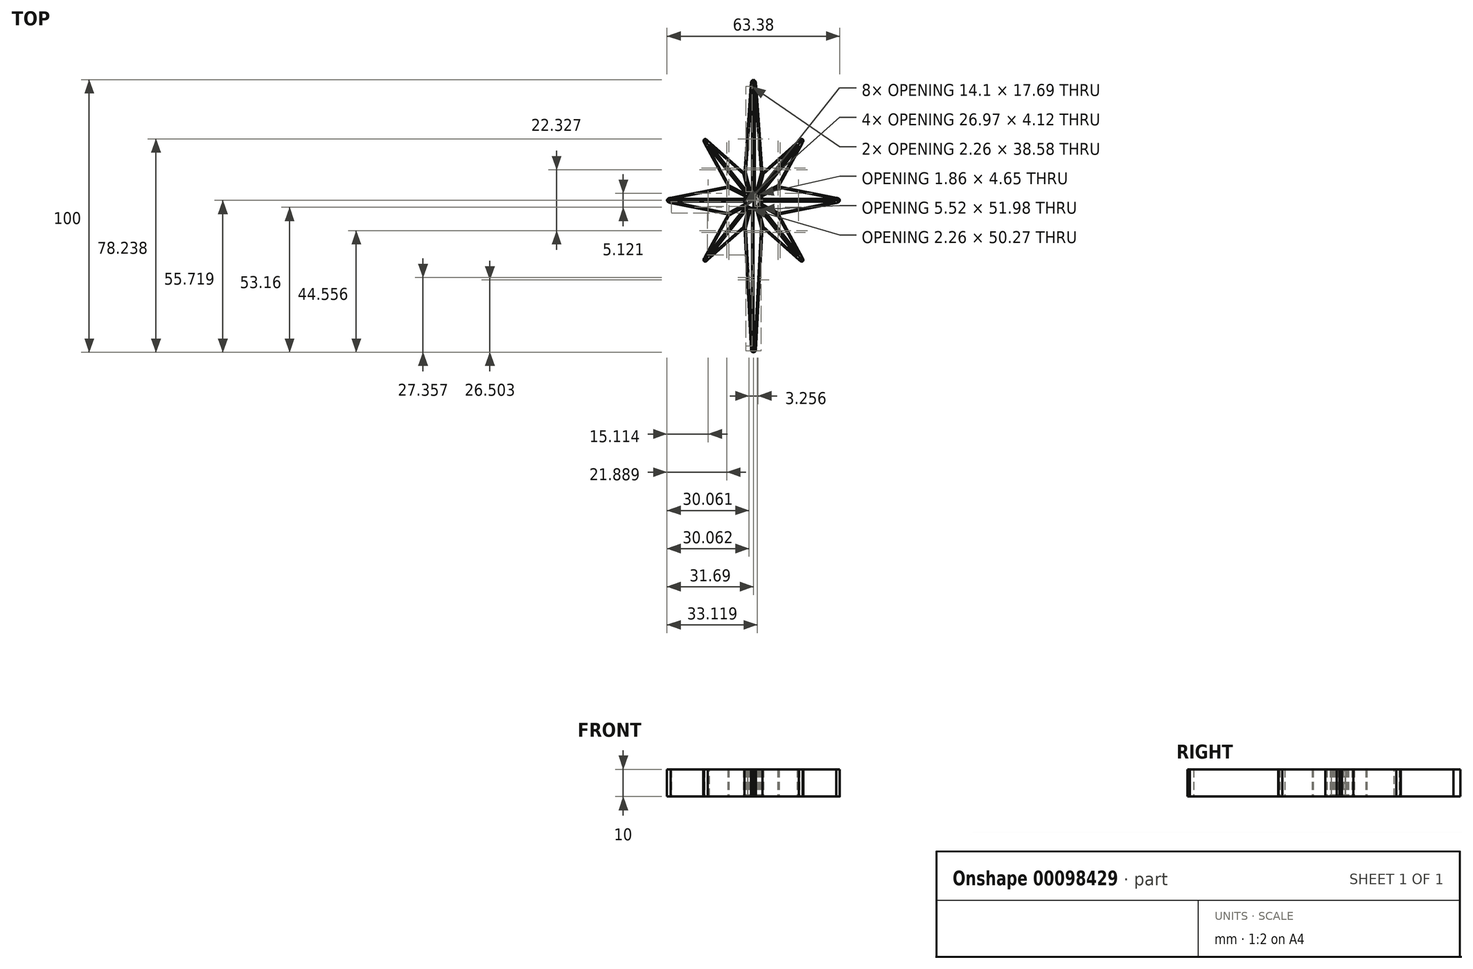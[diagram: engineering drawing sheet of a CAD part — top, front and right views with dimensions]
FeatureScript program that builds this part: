
annotation { "Feature Type Name" : "Feature", "Feature Type Description" : "" }
export const myFeature = defineFeature(function(context is Context, id is Id, definition is map)
    precondition{}
    {
        {
            var Q0;
            Q0=qCreatedBy(makeId("Top.planeOp"),FACE);
            var sketch = newSketch(context, id + "F0", { "sketchPlane" : qUnion([Q0])});
            skFitSpline(sketch, "E0", {"points": [v(0, 44.28) * mm, v(0.72, 43.7) * mm, v(1, 41.85) * mm], "startDerivative": vector(2.03, -1.03) * mm, "endDerivative": vector(0.73, -6.27) * mm});
            skLineSegment(sketch, "E1", {"start": v(1, 41.85) * mm, "end": v(3.26, 9.97) * mm});
            skLineSegment(sketch, "E2", {"start": v(3.26, 9.97) * mm, "end": v(1.35, 2.55) * mm});
            skLineSegment(sketch, "E3", {"start": v(0, -55.72) * mm, "end": v(0, 44.28) * mm});
            skFitSpline(sketch, "E4", {"points": [v(1.35, 2.55) * mm, v(0.8, 2.76) * mm, v(0, 2.88) * mm], "startDerivative": vector(-0.62, 0.31) * mm, "endDerivative": vector(-1.58, 0.08) * mm});
            skCircle(sketch, "E5", {"center": v(0, 0) * mm, "radius": 2.88 * mm});
            skFitSpline(sketch, "E6.MirrorCS", {"points": [v(0, 44.28) * mm, v(-0.72, 43.7) * mm, v(-1, 41.85) * mm], "startDerivative": vector(-2.03, -1.03) * mm, "endDerivative": vector(-0.73, -6.27) * mm});
            skLineSegment(sketch, "E7.MirrorCS", {"start": v(-1, 41.85) * mm, "end": v(-3.26, 9.97) * mm});
            skLineSegment(sketch, "E8.MirrorCS", {"start": v(-3.26, 9.97) * mm, "end": v(-1.35, 2.55) * mm});
            skLineSegment(sketch, "E9", {"start": v(-1.95, 2.12) * mm, "end": v(-18.09, 22.36) * mm});
            skFitSpline(sketch, "E10", {"points": [v(-18.09, 22.36) * mm, v(-17.59, 22.5) * mm, v(-16.7, 21.85) * mm], "startDerivative": vector(1.18, 0.65) * mm, "endDerivative": vector(1.58, -1.52) * mm});
            skLineSegment(sketch, "E11", {"start": v(-16.7, 21.85) * mm, "end": v(-3.26, 9.97) * mm});
            skFitSpline(sketch, "E12.MirrorCS", {"points": [v(-18.09, 22.36) * mm, v(-18.34, 21.9) * mm, v(-17.9, 20.9) * mm], "startDerivative": vector(-0.9, -1) * mm, "endDerivative": vector(1.14, -1.88) * mm});
            skLineSegment(sketch, "E13.MirrorCS", {"start": v(-17.9, 20.9) * mm, "end": v(-9.31, 5.15) * mm});
            skLineSegment(sketch, "E14.MirrorCS", {"start": v(-9.31, 5.15) * mm, "end": v(-2.4, 1.58) * mm});
            skPoint(sketch, "E15.orphan", {"position": v(-2.5, 1.63) * mm});
            skFitSpline(sketch, "E16", {"points": [v(-2.4, 1.58) * mm, v(-2.2, 1.85) * mm, v(-1.95, 2.12) * mm], "startDerivative": vector(0.4, 0.57) * mm, "endDerivative": vector(0.52, 0.51) * mm});
            skLineSegment(sketch, "E17.MirrorCS", {"start": v(16.7, 21.85) * mm, "end": v(3.26, 9.97) * mm});
            skFitSpline(sketch, "E18.MirrorCS", {"points": [v(18.09, 22.36) * mm, v(17.59, 22.5) * mm, v(16.7, 21.85) * mm], "startDerivative": vector(-1.18, 0.65) * mm, "endDerivative": vector(-1.58, -1.52) * mm});
            skFitSpline(sketch, "E19.MirrorCS", {"points": [v(18.09, 22.36) * mm, v(18.34, 21.9) * mm, v(17.9, 20.9) * mm], "startDerivative": vector(0.9, -1) * mm, "endDerivative": vector(-1.14, -1.88) * mm});
            skLineSegment(sketch, "E20.MirrorCS", {"start": v(17.9, 20.9) * mm, "end": v(9.31, 5.15) * mm});
            skLineSegment(sketch, "E21.MirrorCS", {"start": v(1.95, 2.12) * mm, "end": v(18.09, 22.36) * mm});
            skLineSegment(sketch, "E22.MirrorCS", {"start": v(9.31, 5.15) * mm, "end": v(2.4, 1.58) * mm});
            skLineSegment(sketch, "E23.MirrorCS", {"start": v(-9.31, -5.15) * mm, "end": v(-2.4, -1.58) * mm});
            skLineSegment(sketch, "E24.MirrorCS", {"start": v(-1.95, -2.12) * mm, "end": v(-18.09, -22.36) * mm});
            skLineSegment(sketch, "E25.MirrorCS", {"start": v(-17.9, -20.9) * mm, "end": v(-9.31, -5.15) * mm});
            skLineSegment(sketch, "E26.MirrorCS", {"start": v(-16.7, -21.85) * mm, "end": v(-3.26, -9.97) * mm});
            skLineSegment(sketch, "E27.MirrorCS", {"start": v(-3.26, -9.97) * mm, "end": v(-1.35, -2.55) * mm});
            skFitSpline(sketch, "E28.MirrorCS", {"points": [v(-18.09, -22.36) * mm, v(-18.34, -21.9) * mm, v(-17.9, -20.9) * mm], "startDerivative": vector(-0.9, 1) * mm, "endDerivative": vector(1.14, 1.88) * mm});
            skLineSegment(sketch, "E29.MirrorCS", {"start": v(16.7, -21.85) * mm, "end": v(3.26, -9.97) * mm});
            skLineSegment(sketch, "E30.MirrorCS", {"start": v(3.26, -9.97) * mm, "end": v(1.35, -2.55) * mm});
            skLineSegment(sketch, "E31.MirrorCS", {"start": v(1.95, -2.12) * mm, "end": v(18.09, -22.36) * mm});
            skLineSegment(sketch, "E32.MirrorCS", {"start": v(9.31, -5.15) * mm, "end": v(2.4, -1.58) * mm});
            skLineSegment(sketch, "E33.MirrorCS", {"start": v(17.9, -20.9) * mm, "end": v(9.31, -5.15) * mm});
            skFitSpline(sketch, "E34.MirrorCS", {"points": [v(18.09, -22.36) * mm, v(17.59, -22.5) * mm, v(16.7, -21.85) * mm], "startDerivative": vector(-1.18, -0.65) * mm, "endDerivative": vector(-1.58, 1.52) * mm});
            skFitSpline(sketch, "E35.MirrorCS", {"points": [v(18.09, -22.36) * mm, v(18.34, -21.9) * mm, v(17.9, -20.9) * mm], "startDerivative": vector(0.9, 1) * mm, "endDerivative": vector(-1.14, 1.88) * mm});
            skPoint(sketch, "E36.orphan", {"position": v(3.26, -9.97) * mm});
            skFitSpline(sketch, "E37.MirrorCS", {"points": [v(-18.09, -22.36) * mm, v(-17.59, -22.5) * mm, v(-16.7, -21.85) * mm], "startDerivative": vector(1.18, -0.65) * mm, "endDerivative": vector(1.58, 1.52) * mm});
            skLineSegment(sketch, "E38", {"start": v(-9.31, 5.15) * mm, "end": v(-30.36, 0.95) * mm});
            skFitSpline(sketch, "E39", {"points": [v(-30.36, 0.95) * mm, v(-31.49, 0.49) * mm, v(-31.69, 0) * mm, v(-31.67, 0) * mm], "startDerivative": vector(-2.54, -0.48) * mm, "endDerivative": vector(0.26, 0.12) * mm});
            skLineSegment(sketch, "E40", {"start": v(-31.67, 0) * mm, "end": v(-2.88, 0) * mm});
            skLineSegment(sketch, "E41.MirrorCS", {"start": v(-9.31, -5.15) * mm, "end": v(-30.36, -0.95) * mm});
            skFitSpline(sketch, "E42.MirrorCS", {"points": [v(-30.36, -0.95) * mm, v(-31.49, -0.49) * mm, v(-31.69, 0) * mm, v(-31.67, 0) * mm], "startDerivative": vector(-2.54, 0.48) * mm, "endDerivative": vector(0.26, -0.12) * mm});
            skLineSegment(sketch, "E43.MirrorCS", {"start": v(9.31, 5.15) * mm, "end": v(30.36, 0.95) * mm});
            skLineSegment(sketch, "E44.MirrorCS", {"start": v(9.31, -5.15) * mm, "end": v(30.36, -0.95) * mm});
            skFitSpline(sketch, "E45.MirrorCS", {"points": [v(30.36, -0.95) * mm, v(31.49, -0.49) * mm, v(31.69, 0) * mm, v(31.67, 0) * mm], "startDerivative": vector(2.54, 0.48) * mm, "endDerivative": vector(-0.26, -0.12) * mm});
            skFitSpline(sketch, "E46.MirrorCS", {"points": [v(30.36, 0.95) * mm, v(31.49, 0.49) * mm, v(31.69, 0) * mm, v(31.67, 0) * mm], "startDerivative": vector(2.54, -0.48) * mm, "endDerivative": vector(-0.26, 0.12) * mm});
            skLineSegment(sketch, "E47", {"start": v(31.69, 0) * mm, "end": v(2.88, 0) * mm});
            skLineSegment(sketch, "E48", {"start": v(-3.26, -9.97) * mm, "end": v(-0.93, -54.83) * mm});
            skFitSpline(sketch, "E49", {"points": [v(-0.93, -54.83) * mm, v(-0.72, -55.44) * mm, v(0, -55.72) * mm], "startDerivative": vector(0.23, -1.45) * mm, "endDerivative": vector(1.62, -0.34) * mm});
            skFitSpline(sketch, "E50.MirrorCS", {"points": [v(0.93, -54.83) * mm, v(0.72, -55.44) * mm, v(0, -55.72) * mm], "startDerivative": vector(-0.23, -1.45) * mm, "endDerivative": vector(-1.62, -0.34) * mm});
            skLineSegment(sketch, "E51.MirrorCS", {"start": v(3.26, -9.97) * mm, "end": v(0.93, -54.83) * mm});
            skLineSegment(sketch, "E52", {"start": v(0, -2.88) * mm, "end": v(0, -55.72) * mm});
            skSolve(sketch);
        }
        {
            var Q0;
            {var subQ1=sQuery(id+"F0.wireOp",EDGE,"E3");Q0=makeQuery(id+"F0.imprint","IMPRINT",FACE,{"disambiguationData":[TD([[makeQuery(id+"F0.imprint","IMPRINT",EDGE,{"derivedFrom":subQ1}),1.0]])]});}
            var Q1;
            {var subQ1=sQuery(id+"F0.wireOp",EDGE,"E2");Q1=makeQuery(id+"F0.imprint","IMPRINT",FACE,{"disambiguationData":[TD([[makeQuery(id+"F0.imprint","IMPRINT",EDGE,{"derivedFrom":subQ1}),1.0]])]});}
            var Q2;
            {var subQ7=sQuery(id+"F0.wireOp",EDGE,"E22.MirrorCS");Q2=makeQuery(id+"F0.imprint","IMPRINT",FACE,{"disambiguationData":[TD([[makeQuery(id+"F0.imprint","IMPRINT",EDGE,{"derivedFrom":subQ7}),1.0]])]});}
            var Q3;
            {var subQ0=sQuery(id+"F0.wireOp",EDGE,"E30.MirrorCS");Q3=makeQuery(id+"F0.imprint","IMPRINT",FACE,{"disambiguationData":[TD([[makeQuery(id+"F0.imprint","IMPRINT",EDGE,{"derivedFrom":subQ0}),1.0]])]});}
            extrude(context, id + "F1", {"entities" : qUnion([Q0, Q1, Q2, Q3]), "depth" : 10 * mm});
        }
        {
            var Q0;
            {var subQ0=sQuery(id+"F0.wireOp",EDGE,"E16");var subQ1=sQuery(id+"F0.wireOp",EDGE,"E5");var subQ13=makeQuery(id+"F0.imprint","INTERSECT",VERTEX,{"disambiguationData":[OD(0.0)],"derivedFrom":[subQ1,subQ0]});Q0=makeQuery(id+"F0.imprint","IMPRINT",FACE,{"disambiguationData":[TD([[makeQuery(id+"F0.imprint","IMPRINT",EDGE,{"disambiguationData":[TD([[subQ13,-1.0]])],"derivedFrom":subQ1}),1.0]])]});}
            var Q1;
            {var subQ4=sQuery(id+"F0.wireOp",EDGE,"E4");Q1=makeQuery(id+"F0.imprint","IMPRINT",FACE,{"disambiguationData":[TD([[makeQuery(id+"F0.imprint","IMPRINT",EDGE,{"derivedFrom":subQ4}),1.0]])]});}
            extrude(context, id + "F2", {"entities" : qUnion([Q0, Q1]), "depth" : 10 * mm});
        }
        {
            var Q0;
            Q0=makeQuery(id+"F1.opExtrude","CAP_FACE",FACE,{"disambiguationData":[OSD([sQuery(id+"F0.wireOp",EDGE,"E3"),sQuery(id+"F0.wireOp",EDGE,"E5"),sQuery(id+"F0.wireOp",EDGE,"E6.MirrorCS"),sQuery(id+"F0.wireOp",EDGE,"E7.MirrorCS"),sQuery(id+"F0.wireOp",EDGE,"E8.MirrorCS")])],"isStart":false});
            var Q1;
            Q1=makeQuery(id+"F1.opExtrude","CAP_FACE",FACE,{"disambiguationData":[OSD([sQuery(id+"F0.wireOp",EDGE,"E3"),sQuery(id+"F0.wireOp",EDGE,"E5"),sQuery(id+"F0.wireOp",EDGE,"E6.MirrorCS"),sQuery(id+"F0.wireOp",EDGE,"E7.MirrorCS"),sQuery(id+"F0.wireOp",EDGE,"E8.MirrorCS")])],"isStart":true});
            shell(context, id + "F3", {"entities" : qUnion([Q0, Q1]), "thickness" : .5 * mm});
        }
        {
            var Q0;
            {var subQ1=sQuery(id+"F0.wireOp",EDGE,"E0");Q0=makeQuery(id+"F0.imprint","IMPRINT",FACE,{"disambiguationData":[TD([[makeQuery(id+"F0.imprint","IMPRINT",EDGE,{"derivedFrom":subQ1}),-1.0]])]});}
            extrude(context, id + "F4", {"entities" : qUnion([Q0]), "depth" : 10 * mm});
        }
        {
            var Q0;
            Q0=makeQuery(id+"F4.opExtrude","CAP_FACE",FACE,{"disambiguationData":[OSD([sQuery(id+"F0.wireOp",EDGE,"E0"),sQuery(id+"F0.wireOp",EDGE,"E1"),sQuery(id+"F0.wireOp",EDGE,"E2"),sQuery(id+"F0.wireOp",EDGE,"E3"),sQuery(id+"F0.wireOp",EDGE,"E5")])],"isStart":false});
            var Q1;
            Q1=makeQuery(id+"F4.opExtrude","CAP_FACE",FACE,{"disambiguationData":[OSD([sQuery(id+"F0.wireOp",EDGE,"E0"),sQuery(id+"F0.wireOp",EDGE,"E1"),sQuery(id+"F0.wireOp",EDGE,"E2"),sQuery(id+"F0.wireOp",EDGE,"E3"),sQuery(id+"F0.wireOp",EDGE,"E5")])],"isStart":true});
            shell(context, id + "F5", {"entities" : qUnion([Q0, Q1]), "thickness" : .5 * mm});
        }
        {
            var Q0;
            Q0=makeQuery(id+"F1.opExtrude","CAP_FACE",FACE,{"disambiguationData":[OSD([sQuery(id+"F0.wireOp",EDGE,"E2"),sQuery(id+"F0.wireOp",EDGE,"E5"),sQuery(id+"F0.wireOp",EDGE,"E17.MirrorCS"),sQuery(id+"F0.wireOp",EDGE,"E18.MirrorCS"),sQuery(id+"F0.wireOp",EDGE,"E21.MirrorCS")])],"isStart":false});
            var Q1;
            Q1=makeQuery(id+"F1.opExtrude","CAP_FACE",FACE,{"disambiguationData":[OSD([sQuery(id+"F0.wireOp",EDGE,"E2"),sQuery(id+"F0.wireOp",EDGE,"E5"),sQuery(id+"F0.wireOp",EDGE,"E17.MirrorCS"),sQuery(id+"F0.wireOp",EDGE,"E18.MirrorCS"),sQuery(id+"F0.wireOp",EDGE,"E21.MirrorCS")])],"isStart":true});
            shell(context, id + "F6", {"entities" : qUnion([Q0, Q1]), "thickness" : .5 * mm});
        }
        {
            var Q0;
            Q0=makeQuery(id+"F2.opExtrude","CAP_FACE",FACE,{"disambiguationData":[OSD([sQuery(id+"F0.wireOp",EDGE,"E4"),sQuery(id+"F0.wireOp",EDGE,"E5"),sQuery(id+"F0.wireOp",EDGE,"E16")])],"isStart":false});
            var Q1;
            Q1=makeQuery(id+"F2.opExtrude","CAP_FACE",FACE,{"disambiguationData":[OSD([sQuery(id+"F0.wireOp",EDGE,"E4"),sQuery(id+"F0.wireOp",EDGE,"E5"),sQuery(id+"F0.wireOp",EDGE,"E16")])],"isStart":true});
            shell(context, id + "F7", {"entities" : qUnion([Q0, Q1]), "thickness" : .5 * mm});
        }
        {
            var Q0;
            Q0=makeQuery(id+"F0.imprint","IMPRINT",FACE,{"disambiguationData":[TD([[makeQuery(id+"F0.imprint","IMPRINT",EDGE,{"derivedFrom":sQuery(id+"F0.wireOp",EDGE,"E19.MirrorCS")}),-1.0]])]});
            extrude(context, id + "F8", {"entities" : qUnion([Q0]), "depth" : 10 * mm});
        }
        {
            var Q0;
            Q0=makeQuery(id+"F1.opExtrude","CAP_FACE",FACE,{"disambiguationData":[OSD([sQuery(id+"F0.wireOp",EDGE,"E5"),sQuery(id+"F0.wireOp",EDGE,"E22.MirrorCS"),sQuery(id+"F0.wireOp",EDGE,"E43.MirrorCS"),sQuery(id+"F0.wireOp",EDGE,"E45.MirrorCS"),sQuery(id+"F0.wireOp",EDGE,"E46.MirrorCS"),sQuery(id+"F0.wireOp",EDGE,"E47")])],"isStart":false});
            var Q1;
            Q1=makeQuery(id+"F1.opExtrude","CAP_FACE",FACE,{"disambiguationData":[OSD([sQuery(id+"F0.wireOp",EDGE,"E5"),sQuery(id+"F0.wireOp",EDGE,"E22.MirrorCS"),sQuery(id+"F0.wireOp",EDGE,"E43.MirrorCS"),sQuery(id+"F0.wireOp",EDGE,"E45.MirrorCS"),sQuery(id+"F0.wireOp",EDGE,"E46.MirrorCS"),sQuery(id+"F0.wireOp",EDGE,"E47")])],"isStart":true});
            shell(context, id + "F9", {"entities" : qUnion([Q0, Q1]), "thickness" : .5 * mm});
        }
        {
            var Q0;
            Q0=makeQuery(id+"F8.opExtrude","CAP_FACE",FACE,{"disambiguationData":[OSD([sQuery(id+"F0.wireOp",EDGE,"E5"),sQuery(id+"F0.wireOp",EDGE,"E19.MirrorCS"),sQuery(id+"F0.wireOp",EDGE,"E20.MirrorCS"),sQuery(id+"F0.wireOp",EDGE,"E21.MirrorCS"),sQuery(id+"F0.wireOp",EDGE,"E22.MirrorCS")])],"isStart":false});
            var Q1;
            Q1=makeQuery(id+"F8.opExtrude","CAP_FACE",FACE,{"disambiguationData":[OSD([sQuery(id+"F0.wireOp",EDGE,"E5"),sQuery(id+"F0.wireOp",EDGE,"E19.MirrorCS"),sQuery(id+"F0.wireOp",EDGE,"E20.MirrorCS"),sQuery(id+"F0.wireOp",EDGE,"E21.MirrorCS"),sQuery(id+"F0.wireOp",EDGE,"E22.MirrorCS")])],"isStart":true});
            shell(context, id + "F10", {"entities" : qUnion([Q0, Q1]), "thickness" : .5 * mm});
        }
        {
            var Q0;
            {var subQ5=sQuery(id+"F0.wireOp",EDGE,"E32.MirrorCS");Q0=makeQuery(id+"F0.imprint","IMPRINT",FACE,{"disambiguationData":[TD([[makeQuery(id+"F0.imprint","IMPRINT",EDGE,{"derivedFrom":subQ5}),-1.0]])]});}
            extrude(context, id + "F11", {"entities" : qUnion([Q0]), "depth" : 10 * mm});
        }
        {
            var Q0;
            Q0=makeQuery(id+"F11.opExtrude","CAP_FACE",FACE,{"disambiguationData":[OSD([sQuery(id+"F0.wireOp",EDGE,"E5"),sQuery(id+"F0.wireOp",EDGE,"E32.MirrorCS"),sQuery(id+"F0.wireOp",EDGE,"E44.MirrorCS"),sQuery(id+"F0.wireOp",EDGE,"E45.MirrorCS"),sQuery(id+"F0.wireOp",EDGE,"E46.MirrorCS"),sQuery(id+"F0.wireOp",EDGE,"E47")])],"isStart":false});
            var Q1;
            Q1=makeQuery(id+"F11.opExtrude","CAP_FACE",FACE,{"disambiguationData":[OSD([sQuery(id+"F0.wireOp",EDGE,"E5"),sQuery(id+"F0.wireOp",EDGE,"E32.MirrorCS"),sQuery(id+"F0.wireOp",EDGE,"E44.MirrorCS"),sQuery(id+"F0.wireOp",EDGE,"E45.MirrorCS"),sQuery(id+"F0.wireOp",EDGE,"E46.MirrorCS"),sQuery(id+"F0.wireOp",EDGE,"E47")])],"isStart":true});
            shell(context, id + "F12", {"entities" : qUnion([Q0, Q1]), "thickness" : .5 * mm});
        }
        {
            var Q0;
            {var subQ1=sQuery(id+"F0.wireOp",EDGE,"E31.MirrorCS");Q0=makeQuery(id+"F0.imprint","IMPRINT",FACE,{"disambiguationData":[TD([[makeQuery(id+"F0.imprint","IMPRINT",EDGE,{"derivedFrom":subQ1}),1.0]])]});}
            extrude(context, id + "F13", {"entities" : qUnion([Q0]), "depth" : 10 * mm});
        }
        {
            var Q0;
            Q0=makeQuery(id+"F13.opExtrude","CAP_FACE",FACE,{"disambiguationData":[OSD([sQuery(id+"F0.wireOp",EDGE,"E5"),sQuery(id+"F0.wireOp",EDGE,"E31.MirrorCS"),sQuery(id+"F0.wireOp",EDGE,"E32.MirrorCS"),sQuery(id+"F0.wireOp",EDGE,"E33.MirrorCS"),sQuery(id+"F0.wireOp",EDGE,"E35.MirrorCS")])],"isStart":false});
            var Q1;
            Q1=makeQuery(id+"F13.opExtrude","CAP_FACE",FACE,{"disambiguationData":[OSD([sQuery(id+"F0.wireOp",EDGE,"E5"),sQuery(id+"F0.wireOp",EDGE,"E31.MirrorCS"),sQuery(id+"F0.wireOp",EDGE,"E32.MirrorCS"),sQuery(id+"F0.wireOp",EDGE,"E33.MirrorCS"),sQuery(id+"F0.wireOp",EDGE,"E35.MirrorCS")])],"isStart":true});
            shell(context, id + "F14", {"entities" : qUnion([Q0, Q1]), "thickness" : .5 * mm});
        }
        {
            var Q0;
            Q0=makeQuery(id+"F0.imprint","IMPRINT",FACE,{"disambiguationData":[TD([[makeQuery(id+"F0.imprint","IMPRINT",EDGE,{"derivedFrom":sQuery(id+"F0.wireOp",EDGE,"E29.MirrorCS")}),-1.0]])]});
            extrude(context, id + "F15", {"entities" : qUnion([Q0]), "depth" : 10 * mm});
        }
        {
            var Q0;
            Q0=makeQuery(id+"F15.opExtrude","CAP_FACE",FACE,{"disambiguationData":[OSD([sQuery(id+"F0.wireOp",EDGE,"E5"),sQuery(id+"F0.wireOp",EDGE,"E29.MirrorCS"),sQuery(id+"F0.wireOp",EDGE,"E30.MirrorCS"),sQuery(id+"F0.wireOp",EDGE,"E31.MirrorCS"),sQuery(id+"F0.wireOp",EDGE,"E34.MirrorCS")])],"isStart":false});
            var Q1;
            Q1=makeQuery(id+"F15.opExtrude","CAP_FACE",FACE,{"disambiguationData":[OSD([sQuery(id+"F0.wireOp",EDGE,"E5"),sQuery(id+"F0.wireOp",EDGE,"E29.MirrorCS"),sQuery(id+"F0.wireOp",EDGE,"E30.MirrorCS"),sQuery(id+"F0.wireOp",EDGE,"E31.MirrorCS"),sQuery(id+"F0.wireOp",EDGE,"E34.MirrorCS")])],"isStart":true});
            shell(context, id + "F16", {"entities" : qUnion([Q0, Q1]), "thickness" : .5 * mm});
        }
        {
            var Q0;
            Q0=makeQuery(id+"F1.opExtrude","CAP_FACE",FACE,{"disambiguationData":[OSD([sQuery(id+"F0.wireOp",EDGE,"E5"),sQuery(id+"F0.wireOp",EDGE,"E30.MirrorCS"),sQuery(id+"F0.wireOp",EDGE,"E50.MirrorCS"),sQuery(id+"F0.wireOp",EDGE,"E51.MirrorCS"),sQuery(id+"F0.wireOp",EDGE,"E52")])],"isStart":false});
            var Q1;
            Q1=makeQuery(id+"F1.opExtrude","CAP_FACE",FACE,{"disambiguationData":[OSD([sQuery(id+"F0.wireOp",EDGE,"E5"),sQuery(id+"F0.wireOp",EDGE,"E30.MirrorCS"),sQuery(id+"F0.wireOp",EDGE,"E50.MirrorCS"),sQuery(id+"F0.wireOp",EDGE,"E51.MirrorCS"),sQuery(id+"F0.wireOp",EDGE,"E52")])],"isStart":true});
            shell(context, id + "F17", {"entities" : qUnion([Q0, Q1]), "thickness" : .5 * mm});
        }
        {
            var Q0;
            {var subQ0=sQuery(id+"F0.wireOp",EDGE,"E27.MirrorCS");Q0=makeQuery(id+"F0.imprint","IMPRINT",FACE,{"disambiguationData":[TD([[makeQuery(id+"F0.imprint","IMPRINT",EDGE,{"derivedFrom":subQ0}),-1.0]])]});}
            var Q1;
            {var subQ0=sQuery(id+"F0.wireOp",EDGE,"E24.MirrorCS");Q1=makeQuery(id+"F0.imprint","IMPRINT",FACE,{"disambiguationData":[TD([[makeQuery(id+"F0.imprint","IMPRINT",EDGE,{"derivedFrom":subQ0}),-1.0]])]});}
            var Q2;
            {var subQ4=sQuery(id+"F0.wireOp",EDGE,"E14.MirrorCS");Q2=makeQuery(id+"F0.imprint","IMPRINT",FACE,{"disambiguationData":[TD([[makeQuery(id+"F0.imprint","IMPRINT",EDGE,{"derivedFrom":subQ4}),-1.0]])]});}
            var Q3;
            {var subQ1=sQuery(id+"F0.wireOp",EDGE,"E8.MirrorCS");Q3=makeQuery(id+"F0.imprint","IMPRINT",FACE,{"disambiguationData":[TD([[makeQuery(id+"F0.imprint","IMPRINT",EDGE,{"derivedFrom":subQ1}),-1.0]])]});}
            extrude(context, id + "F18", {"entities" : qUnion([Q0, Q1, Q2, Q3]), "depth" : 10 * mm});
        }
        {
            var Q0;
            Q0=makeQuery(id+"F18.opExtrude","CAP_FACE",FACE,{"disambiguationData":[OSD([sQuery(id+"F0.wireOp",EDGE,"E5"),sQuery(id+"F0.wireOp",EDGE,"E14.MirrorCS"),sQuery(id+"F0.wireOp",EDGE,"E38"),sQuery(id+"F0.wireOp",EDGE,"E39"),sQuery(id+"F0.wireOp",EDGE,"E40"),sQuery(id+"F0.wireOp",EDGE,"E42.MirrorCS")])],"isStart":false});
            var Q1;
            Q1=makeQuery(id+"F18.opExtrude","CAP_FACE",FACE,{"disambiguationData":[OSD([sQuery(id+"F0.wireOp",EDGE,"E5"),sQuery(id+"F0.wireOp",EDGE,"E8.MirrorCS"),sQuery(id+"F0.wireOp",EDGE,"E9"),sQuery(id+"F0.wireOp",EDGE,"E10"),sQuery(id+"F0.wireOp",EDGE,"E11")])],"isStart":false});
            var Q2;
            Q2=makeQuery(id+"F18.opExtrude","CAP_FACE",FACE,{"disambiguationData":[OSD([sQuery(id+"F0.wireOp",EDGE,"E5"),sQuery(id+"F0.wireOp",EDGE,"E24.MirrorCS"),sQuery(id+"F0.wireOp",EDGE,"E25.MirrorCS"),sQuery(id+"F0.wireOp",EDGE,"E28.MirrorCS"),sQuery(id+"F0.wireOp",EDGE,"E23.MirrorCS")])],"isStart":false});
            var Q3;
            Q3=makeQuery(id+"F18.opExtrude","CAP_FACE",FACE,{"disambiguationData":[OSD([sQuery(id+"F0.wireOp",EDGE,"E5"),sQuery(id+"F0.wireOp",EDGE,"E27.MirrorCS"),sQuery(id+"F0.wireOp",EDGE,"E48"),sQuery(id+"F0.wireOp",EDGE,"E49"),sQuery(id+"F0.wireOp",EDGE,"E52")])],"isStart":false});
            var Q4;
            Q4=makeQuery(id+"F18.opExtrude","CAP_FACE",FACE,{"disambiguationData":[OSD([sQuery(id+"F0.wireOp",EDGE,"E5"),sQuery(id+"F0.wireOp",EDGE,"E24.MirrorCS"),sQuery(id+"F0.wireOp",EDGE,"E25.MirrorCS"),sQuery(id+"F0.wireOp",EDGE,"E28.MirrorCS"),sQuery(id+"F0.wireOp",EDGE,"E23.MirrorCS")])],"isStart":true});
            var Q5;
            Q5=makeQuery(id+"F18.opExtrude","CAP_FACE",FACE,{"disambiguationData":[OSD([sQuery(id+"F0.wireOp",EDGE,"E5"),sQuery(id+"F0.wireOp",EDGE,"E14.MirrorCS"),sQuery(id+"F0.wireOp",EDGE,"E38"),sQuery(id+"F0.wireOp",EDGE,"E39"),sQuery(id+"F0.wireOp",EDGE,"E40"),sQuery(id+"F0.wireOp",EDGE,"E42.MirrorCS")])],"isStart":true});
            var Q6;
            Q6=makeQuery(id+"F18.opExtrude","CAP_FACE",FACE,{"disambiguationData":[OSD([sQuery(id+"F0.wireOp",EDGE,"E5"),sQuery(id+"F0.wireOp",EDGE,"E8.MirrorCS"),sQuery(id+"F0.wireOp",EDGE,"E9"),sQuery(id+"F0.wireOp",EDGE,"E10"),sQuery(id+"F0.wireOp",EDGE,"E11")])],"isStart":true});
            var Q7;
            Q7=makeQuery(id+"F18.opExtrude","CAP_FACE",FACE,{"disambiguationData":[OSD([sQuery(id+"F0.wireOp",EDGE,"E5"),sQuery(id+"F0.wireOp",EDGE,"E27.MirrorCS"),sQuery(id+"F0.wireOp",EDGE,"E48"),sQuery(id+"F0.wireOp",EDGE,"E49"),sQuery(id+"F0.wireOp",EDGE,"E52")])],"isStart":true});
            shell(context, id + "F19", {"entities" : qUnion([Q0, Q1, Q2, Q3, Q4, Q5, Q6, Q7]), "thickness" : .5 * mm});
        }
        {
            var Q0;
            {var subQ0=sQuery(id+"F0.wireOp",EDGE,"E9");Q0=makeQuery(id+"F0.imprint","IMPRINT",FACE,{"disambiguationData":[TD([[makeQuery(id+"F0.imprint","IMPRINT",EDGE,{"derivedFrom":subQ0}),1.0]])]});}
            var Q1;
            {var subQ1=sQuery(id+"F0.wireOp",EDGE,"E40");Q1=makeQuery(id+"F0.imprint","IMPRINT",FACE,{"disambiguationData":[TD([[makeQuery(id+"F0.imprint","IMPRINT",EDGE,{"derivedFrom":subQ1}),-1.0]])]});}
            var Q2;
            {var subQ1=sQuery(id+"F0.wireOp",EDGE,"E24.MirrorCS");Q2=makeQuery(id+"F0.imprint","IMPRINT",FACE,{"disambiguationData":[TD([[makeQuery(id+"F0.imprint","IMPRINT",EDGE,{"derivedFrom":subQ1}),1.0]])]});}
            extrude(context, id + "F20", {"entities" : qUnion([Q0, Q1, Q2]), "depth" : 10 * mm});
        }
        {
            var Q0;
            Q0=makeQuery(id+"F20.opExtrude","CAP_FACE",FACE,{"disambiguationData":[OSD([sQuery(id+"F0.wireOp",EDGE,"E5"),sQuery(id+"F0.wireOp",EDGE,"E9"),sQuery(id+"F0.wireOp",EDGE,"E12.MirrorCS"),sQuery(id+"F0.wireOp",EDGE,"E13.MirrorCS"),sQuery(id+"F0.wireOp",EDGE,"E14.MirrorCS"),sQuery(id+"F0.wireOp",EDGE,"E16")])],"isStart":false});
            var Q1;
            Q1=makeQuery(id+"F20.opExtrude","CAP_FACE",FACE,{"disambiguationData":[OSD([sQuery(id+"F0.wireOp",EDGE,"E5"),sQuery(id+"F0.wireOp",EDGE,"E39"),sQuery(id+"F0.wireOp",EDGE,"E40"),sQuery(id+"F0.wireOp",EDGE,"E41.MirrorCS"),sQuery(id+"F0.wireOp",EDGE,"E23.MirrorCS"),sQuery(id+"F0.wireOp",EDGE,"E42.MirrorCS")])],"isStart":false});
            var Q2;
            Q2=makeQuery(id+"F20.opExtrude","CAP_FACE",FACE,{"disambiguationData":[OSD([sQuery(id+"F0.wireOp",EDGE,"E5"),sQuery(id+"F0.wireOp",EDGE,"E24.MirrorCS"),sQuery(id+"F0.wireOp",EDGE,"E26.MirrorCS"),sQuery(id+"F0.wireOp",EDGE,"E27.MirrorCS"),sQuery(id+"F0.wireOp",EDGE,"E37.MirrorCS")])],"isStart":false});
            var Q3;
            Q3=makeQuery(id+"F20.opExtrude","CAP_FACE",FACE,{"disambiguationData":[OSD([sQuery(id+"F0.wireOp",EDGE,"E5"),sQuery(id+"F0.wireOp",EDGE,"E24.MirrorCS"),sQuery(id+"F0.wireOp",EDGE,"E26.MirrorCS"),sQuery(id+"F0.wireOp",EDGE,"E27.MirrorCS"),sQuery(id+"F0.wireOp",EDGE,"E37.MirrorCS")])],"isStart":true});
            var Q4;
            Q4=makeQuery(id+"F20.opExtrude","CAP_FACE",FACE,{"disambiguationData":[OSD([sQuery(id+"F0.wireOp",EDGE,"E5"),sQuery(id+"F0.wireOp",EDGE,"E39"),sQuery(id+"F0.wireOp",EDGE,"E40"),sQuery(id+"F0.wireOp",EDGE,"E41.MirrorCS"),sQuery(id+"F0.wireOp",EDGE,"E23.MirrorCS"),sQuery(id+"F0.wireOp",EDGE,"E42.MirrorCS")])],"isStart":true});
            var Q5;
            Q5=makeQuery(id+"F20.opExtrude","CAP_FACE",FACE,{"disambiguationData":[OSD([sQuery(id+"F0.wireOp",EDGE,"E5"),sQuery(id+"F0.wireOp",EDGE,"E9"),sQuery(id+"F0.wireOp",EDGE,"E12.MirrorCS"),sQuery(id+"F0.wireOp",EDGE,"E13.MirrorCS"),sQuery(id+"F0.wireOp",EDGE,"E14.MirrorCS"),sQuery(id+"F0.wireOp",EDGE,"E16")])],"isStart":true});
            shell(context, id + "F21", {"entities" : qUnion([Q0, Q1, Q2, Q3, Q4, Q5]), "thickness" : .5 * mm});
        }
    });
